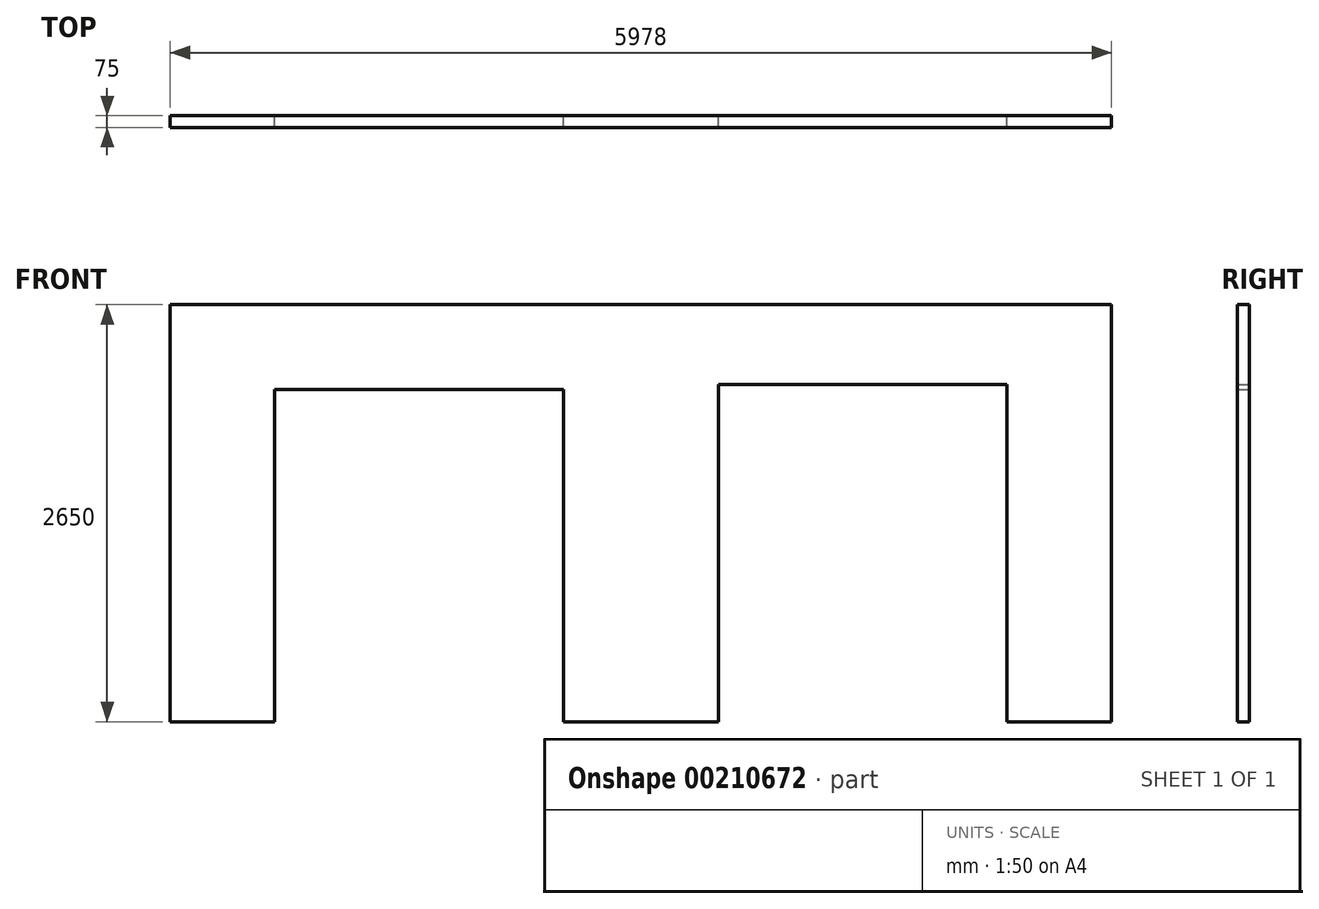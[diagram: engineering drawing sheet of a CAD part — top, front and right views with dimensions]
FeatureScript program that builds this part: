
annotation { "Feature Type Name" : "Feature", "Feature Type Description" : "" }
export const myFeature = defineFeature(function(context is Context, id is Id, definition is map)
    precondition{}
    {
        {
            var Q0;
            Q0=qCreatedBy(makeId("Front.planeOp"),FACE);
            var sketch = newSketch(context, id + "F0", { "sketchPlane" : qUnion([Q0])});
            skLineSegment(sketch, "E0.bottom", {"start": v(0, 0) * mm, "end": v(5978, 0) * mm});
            skLineSegment(sketch, "E0.top", {"start": v(0, 2650) * mm, "end": v(5978, 2650) * mm});
            skLineSegment(sketch, "E0.left", {"start": v(0, 0) * mm, "end": v(0, 2650) * mm});
            skLineSegment(sketch, "E0.right", {"start": v(5978, 0) * mm, "end": v(5978, 2650) * mm});
            skLineSegment(sketch, "E1.bottom", {"start": v(663, 0) * mm, "end": v(2497, 0) * mm});
            skLineSegment(sketch, "E1.top", {"start": v(663, 2112) * mm, "end": v(2497, 2112) * mm});
            skLineSegment(sketch, "E1.left", {"start": v(663, 0) * mm, "end": v(663, 2112) * mm});
            skLineSegment(sketch, "E1.right", {"start": v(2497, 0) * mm, "end": v(2497, 2112) * mm});
            skLineSegment(sketch, "E2.bottom", {"start": v(3481, 0) * mm, "end": v(5315, 0) * mm});
            skLineSegment(sketch, "E2.top", {"start": v(3481, 2142) * mm, "end": v(5315, 2142) * mm});
            skLineSegment(sketch, "E2.left", {"start": v(3481, 0) * mm, "end": v(3481, 2142) * mm});
            skLineSegment(sketch, "E2.right", {"start": v(5315, 0) * mm, "end": v(5315, 2142) * mm});
            skSolve(sketch);
        }
        {
            var Q0;
            Q0=makeQuery(id+"F0.imprint","IMPRINT",FACE,{"disambiguationData":[TD([[makeQuery(id+"F0.imprint","IMPRINT",EDGE,{"derivedFrom":sQuery(id+"F0.wireOp",EDGE,"E0.bottom")}),1.0]])]});
            extrude(context, id + "F1", {"entities" : qUnion([Q0]), "depth" : 75 * mm});
        }
    });
